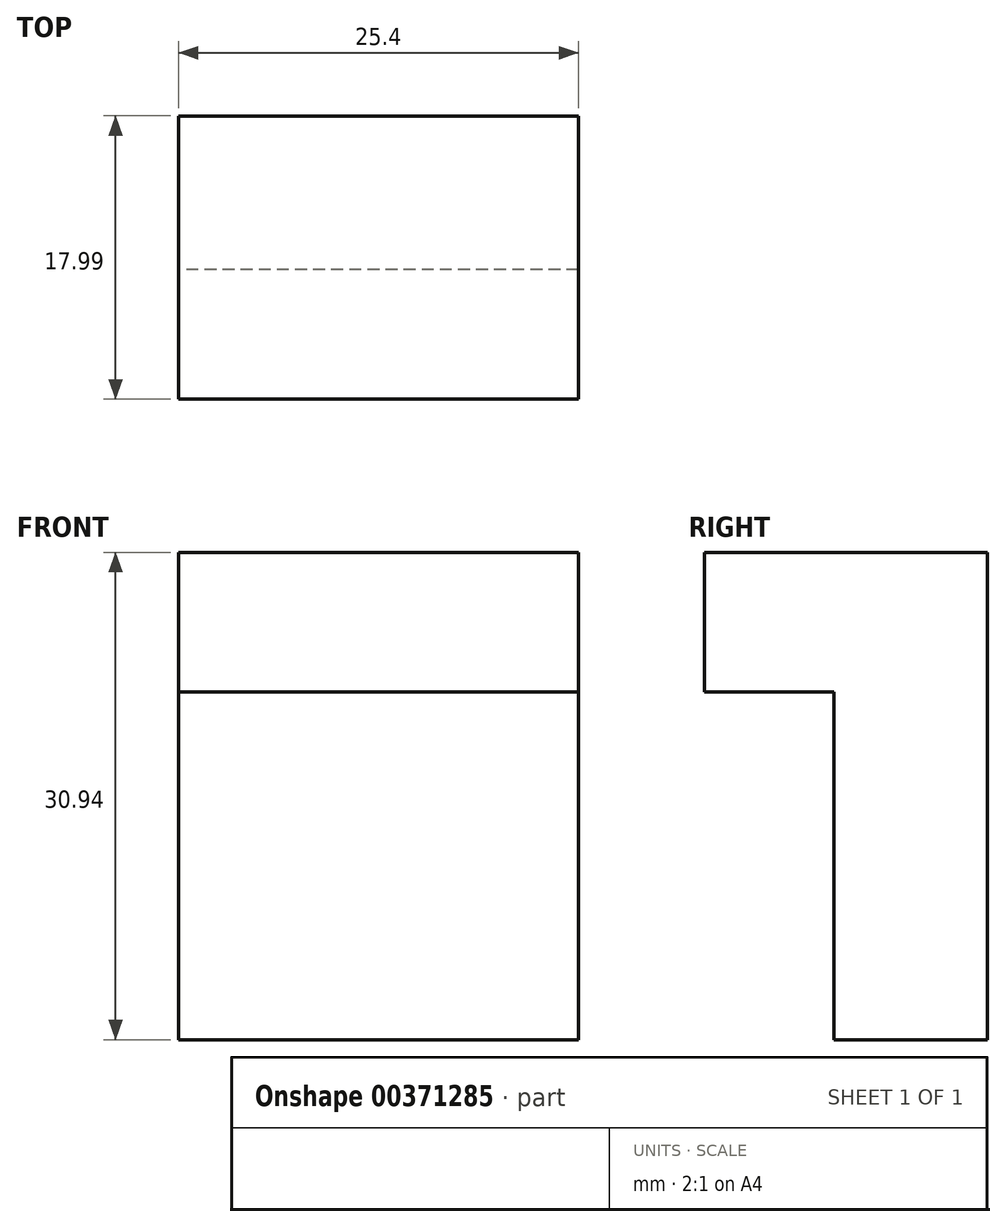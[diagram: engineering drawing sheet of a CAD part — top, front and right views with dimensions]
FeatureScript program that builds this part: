
annotation { "Feature Type Name" : "Feature", "Feature Type Description" : "" }
export const myFeature = defineFeature(function(context is Context, id is Id, definition is map)
    precondition{}
    {
        {
            var Q0;
            Q0=qCreatedBy(makeId("Right.planeOp"),FACE);
            var sketch = newSketch(context, id + "F0", { "sketchPlane" : qUnion([Q0])});
            skLineSegment(sketch, "E0", {"start": v(11.58, 0) * mm, "end": v(11.58, 22.1) * mm});
            skLineSegment(sketch, "E1", {"start": v(11.58, 22.1) * mm, "end": v(3.35, 22.1) * mm});
            skLineSegment(sketch, "E2", {"start": v(3.35, 21.49) * mm, "end": v(3.35, 30.94) * mm});
            skLineSegment(sketch, "E3", {"start": v(3.35, 30.94) * mm, "end": v(29.57, 30.94) * mm});
            skLineSegment(sketch, "E4", {"start": v(29.57, 30.94) * mm, "end": v(29.57, 22.1) * mm});
            skLineSegment(sketch, "E5", {"start": v(29.57, 22.1) * mm, "end": v(21.34, 22.1) * mm});
            skLineSegment(sketch, "E6", {"start": v(21.34, 22.1) * mm, "end": v(21.34, 0) * mm});
            skLineSegment(sketch, "E7", {"start": v(21.34, 0) * mm, "end": v(11.58, 0) * mm});
            skSolve(sketch);
        }
        {
            var Q0;
            Q0=makeQuery(id+"F0.imprint","IMPRINT",FACE,{"disambiguationData":[TD([[makeQuery(id+"F0.imprint","IMPRINT",EDGE,{"derivedFrom":sQuery(id+"F0.wireOp",EDGE,"E0")}),-1.0]])]});
            extrude(context, id + "F1", {"entities" : qUnion([Q0]), "depth" : 25.4 * mm});
        }
        {
            var Q0;
            Q0=makeQuery(id+"F1.opExtrude","SWEPT_FACE",FACE,{"disambiguationData":[OSD([sQuery(id+"F0.wireOp",EDGE,"E5")])]});
            extrude(context, id + "F2", {"entities" : qUnion([Q0]), "operationType" : NewBodyOperationType.REMOVE, "oppositeDirection" : true, "depth" : 25.4 * mm});
        }
    });
